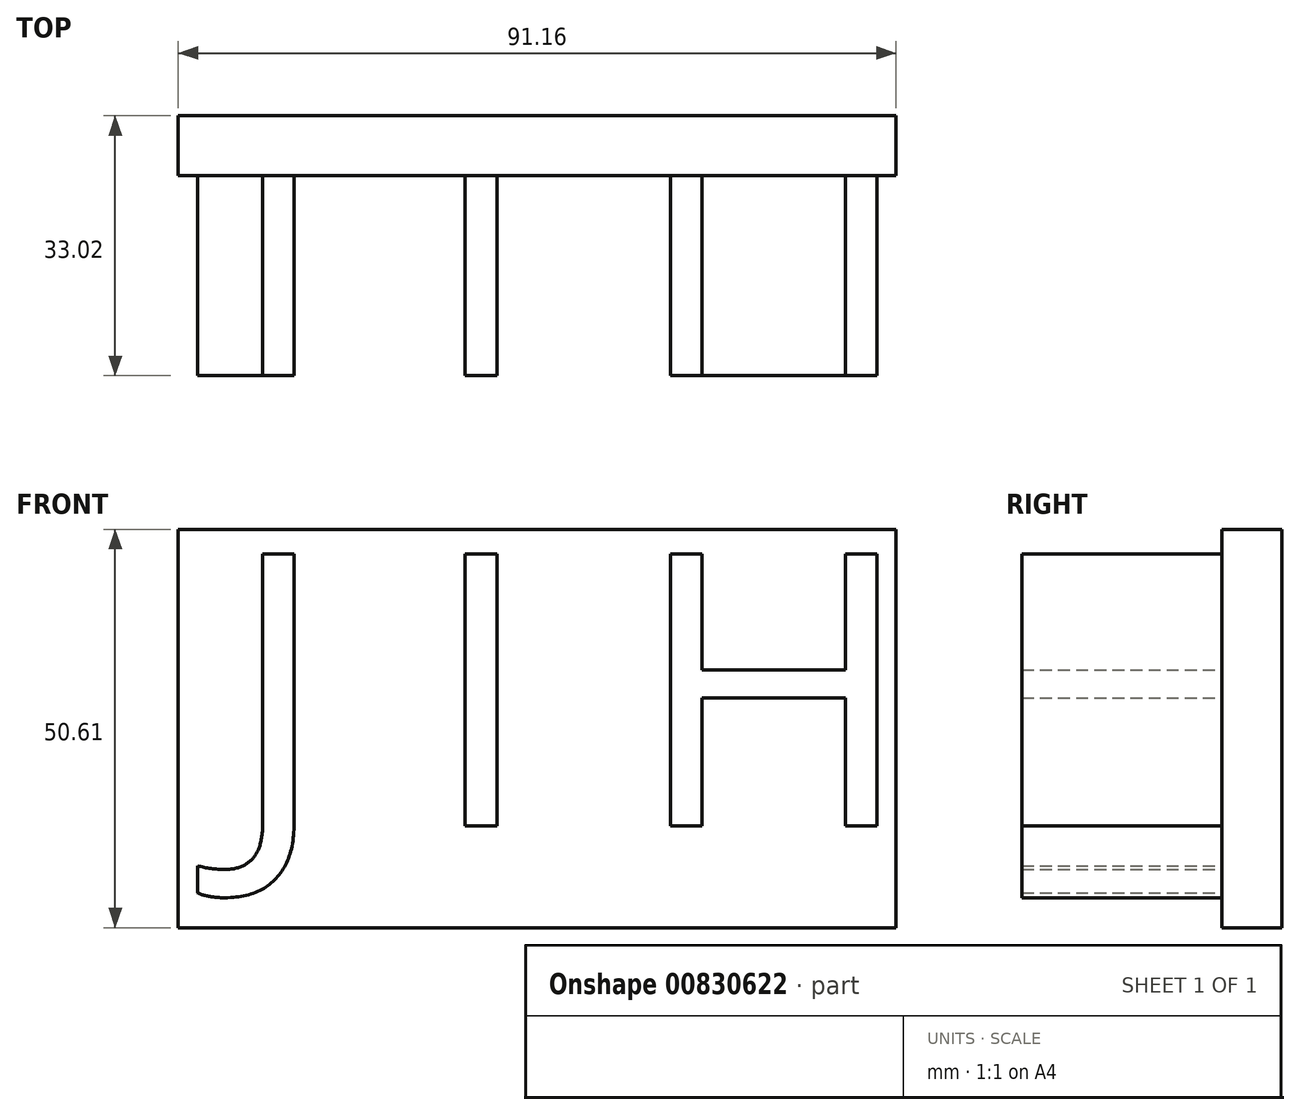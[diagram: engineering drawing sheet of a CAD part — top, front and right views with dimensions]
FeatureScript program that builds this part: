
annotation { "Feature Type Name" : "Feature", "Feature Type Description" : "" }
export const myFeature = defineFeature(function(context is Context, id is Id, definition is map)
    precondition{}
    {
        {
            var Q0;
            Q0=qCreatedBy(makeId("Front.planeOp"),FACE);
            var sketch = newSketch(context, id + "F0", { "sketchPlane" : qUnion([Q0])});
            skLineSegment(sketch, "E0.bottom", {"start": v(0, 50.6) * mm, "end": v(91.16, 50.6) * mm});
            skLineSegment(sketch, "E0.top", {"start": v(0, 0) * mm, "end": v(91.16, 0) * mm});
            skLineSegment(sketch, "E0.left", {"start": v(0, 50.6) * mm, "end": v(0, 0) * mm});
            skLineSegment(sketch, "E0.right", {"start": v(91.16, 50.6) * mm, "end": v(91.16, 0) * mm});
            skSolve(sketch);
        }
        {
            var Q0;
            Q0 = qSketchRegion(id + "FMjWgvcwXOHGY0J_0", true);
            var Q1;
            Q1=makeQuery(id+"F0.imprint","IMPRINT",FACE,{"disambiguationData":[TD([[makeQuery(id+"F0.imprint","IMPRINT",EDGE,{"derivedFrom":sQuery(id+"F0.wireOp",EDGE,"E0.bottom")}),-1.0]])]});
            extrude(context, id + "F1", {"entities" : qUnion([Q0, Q1]), "depth" : 7.62 * mm, "offsetDistance" : 25.4 * mm});
        }
        {
            var Q0;
            Q0=makeQuery(id+"F1.opExtrude","CAP_FACE",FACE,{"disambiguationData":[OSD([sQuery(id+"F0.wireOp",EDGE,"E0.bottom"),sQuery(id+"F0.wireOp",EDGE,"E0.top"),sQuery(id+"F0.wireOp",EDGE,"E0.left"),sQuery(id+"F0.wireOp",EDGE,"E0.right")])],"isStart":false});
            var sketch = newSketch(context, id + "F2", { "sketchPlane" : qUnion([Q0])});
            skText(sketch, "E1", { "text": "J I H", "fontName": "OpenSans-Regular.ttf"});
            const initialGuessF2  = {"E1": [0.0062, 0.0129, 1, 0, 0.03484]};
            skSetInitialGuess(sketch, initialGuessF2);
            skSolve(sketch);
        }
        {
            var Q0;
            Q0=makeQuery(id+"F2.imprint","IMPRINT",FACE,{"disambiguationData":[TD([[makeQuery(id+"F2.imprint","IMPRINT",EDGE,{"derivedFrom":sQuery(id+"F2.wireOp",EDGE,"E1.sketch_text.stroke-10")}),-1.0]])]});
            var Q1;
            Q1=makeQuery(id+"F2.imprint","IMPRINT",FACE,{"disambiguationData":[TD([[makeQuery(id+"F2.imprint","IMPRINT",EDGE,{"derivedFrom":sQuery(id+"F2.wireOp",EDGE,"E1.sketch_text.stroke-0")}),-1.0]])]});
            var Q2;
            Q2=makeQuery(id+"F2.imprint","IMPRINT",FACE,{"disambiguationData":[TD([[makeQuery(id+"F2.imprint","IMPRINT",EDGE,{"derivedFrom":sQuery(id+"F2.wireOp",EDGE,"E1.sketch_text.stroke-14")}),-1.0]])]});
            extrude(context, id + "F3", {"entities" : qUnion([Q0, Q1, Q2]), "operationType" : NewBodyOperationType.ADD, "depth" : 25.4 * mm, "offsetDistance" : 25.4 * mm});
        }
    });
